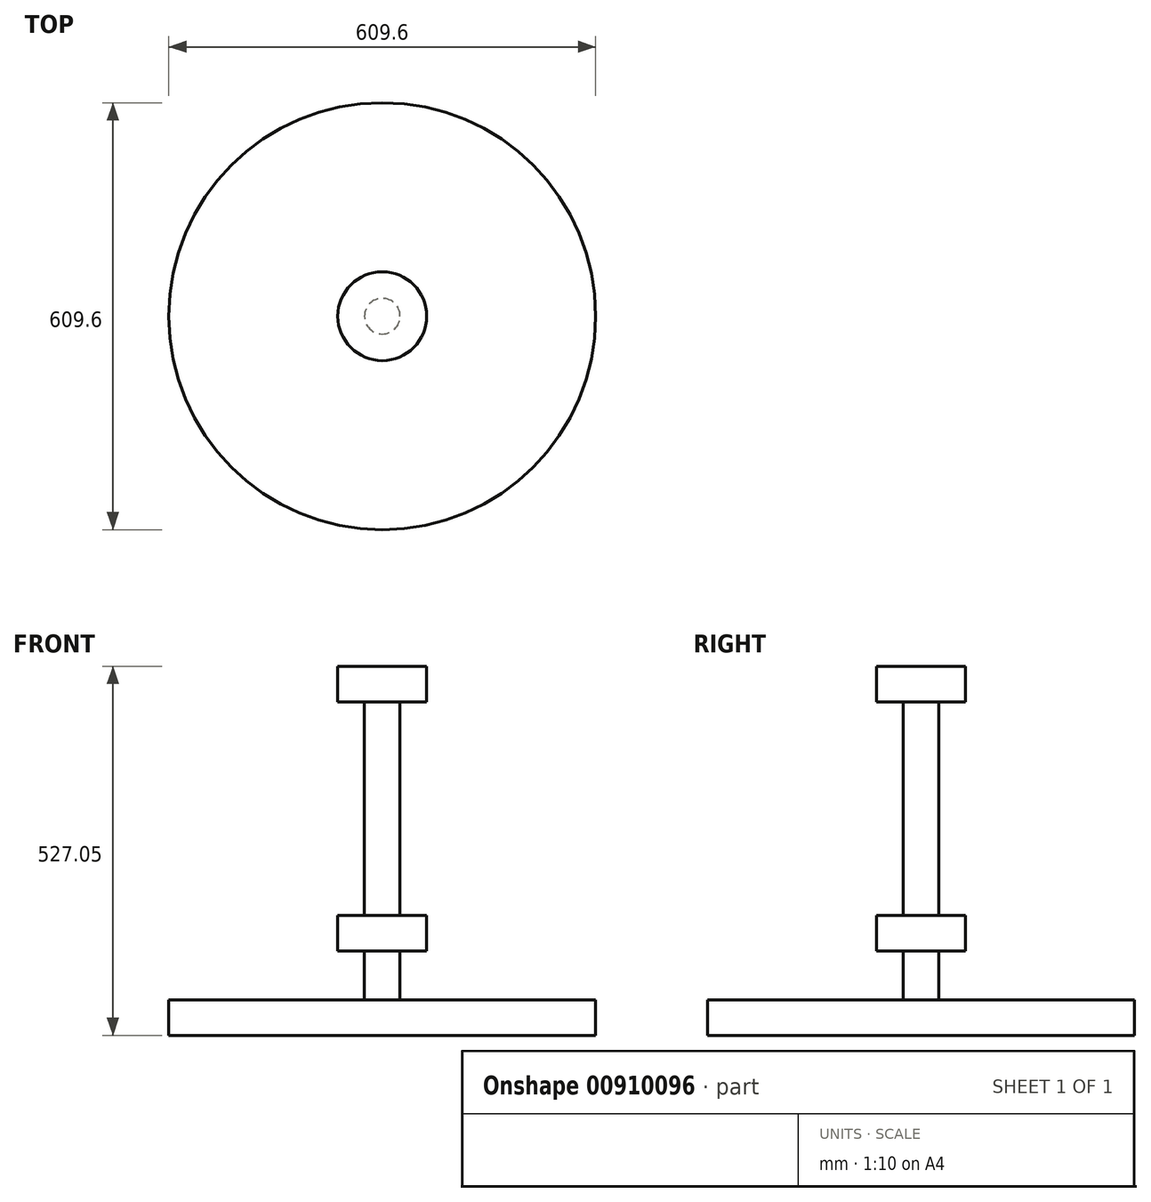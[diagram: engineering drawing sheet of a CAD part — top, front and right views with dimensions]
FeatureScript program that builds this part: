
annotation { "Feature Type Name" : "Feature", "Feature Type Description" : "" }
export const myFeature = defineFeature(function(context is Context, id is Id, definition is map)
    precondition{}
    {
        {
            var Q0;
            Q0=qCreatedBy(makeId("Front.planeOp"),FACE);
            var sketch = newSketch(context, id + "F0", { "sketchPlane" : qUnion([Q0])});
            skLineSegment(sketch, "E0.left", {"start": v(25.4, -152.4) * mm, "end": v(25.4, -88.9) * mm});
            skLineSegment(sketch, "E0.right", {"start": v(0, -152.4) * mm, "end": v(0, 152.4) * mm});
            skLineSegment(sketch, "E1.bottom", {"start": v(25.4, 152.4) * mm, "end": v(63.5, 152.4) * mm});
            skLineSegment(sketch, "E1.top", {"start": v(0, 203.2) * mm, "end": v(63.5, 203.2) * mm});
            skLineSegment(sketch, "E1.left", {"start": v(0, 152.4) * mm, "end": v(0, 203.2) * mm});
            skLineSegment(sketch, "E1.right", {"start": v(63.5, 152.4) * mm, "end": v(63.5, 203.2) * mm});
            skLineSegment(sketch, "E2.bottom", {"start": v(25.4, -152.4) * mm, "end": v(63.5, -152.4) * mm});
            skLineSegment(sketch, "E2.top", {"start": v(0, -203.2) * mm, "end": v(63.5, -203.2) * mm});
            skLineSegment(sketch, "E2.left", {"start": v(0, -152.4) * mm, "end": v(0, -203.2) * mm});
            skLineSegment(sketch, "E2.right", {"start": v(63.5, -152.4) * mm, "end": v(63.5, -203.2) * mm});
            skLineSegment(sketch, "E3.trimOffspring", {"start": v(25.4, -76.2) * mm, "end": v(25.4, 152.4) * mm});
            skLineSegment(sketch, "E4", {"start": v(25.4, -76.2) * mm, "end": v(25.4, -88.9) * mm});
            skLineSegment(sketch, "E5.bottom", {"start": v(0, -323.85) * mm, "end": v(304.8, -323.85) * mm});
            skLineSegment(sketch, "E5.top", {"start": v(0, -273.05) * mm, "end": v(304.8, -273.05) * mm});
            skLineSegment(sketch, "E5.left", {"start": v(0, -323.85) * mm, "end": v(0, -273.05) * mm});
            skLineSegment(sketch, "E5.right", {"start": v(304.8, -323.85) * mm, "end": v(304.8, -273.05) * mm});
            skLineSegment(sketch, "E6.bottom", {"start": v(0, -203.2) * mm, "end": v(25.4, -203.2) * mm});
            skLineSegment(sketch, "E6.top", {"start": v(0, -273.05) * mm, "end": v(25.4, -273.05) * mm});
            skLineSegment(sketch, "E6.left", {"start": v(0, -203.2) * mm, "end": v(0, -273.05) * mm});
            skLineSegment(sketch, "E6.right", {"start": v(25.4, -203.2) * mm, "end": v(25.4, -273.05) * mm});
            skSolve(sketch);
        }
        {
            var Q0;
            Q0 = qSketchRegion(id + "F0", true);
            var Q1;
            Q1=sQuery(id+"F0.wireOp",EDGE,"E0.right");
            revolve(context, id + "F1", {"surfaceOperationType" : NewSurfaceOperationType.NEW, "entities" : qUnion([Q0]), "axis" : qUnion([Q1]), "revolveType" : RevolveType.FULL});
        }
    });
